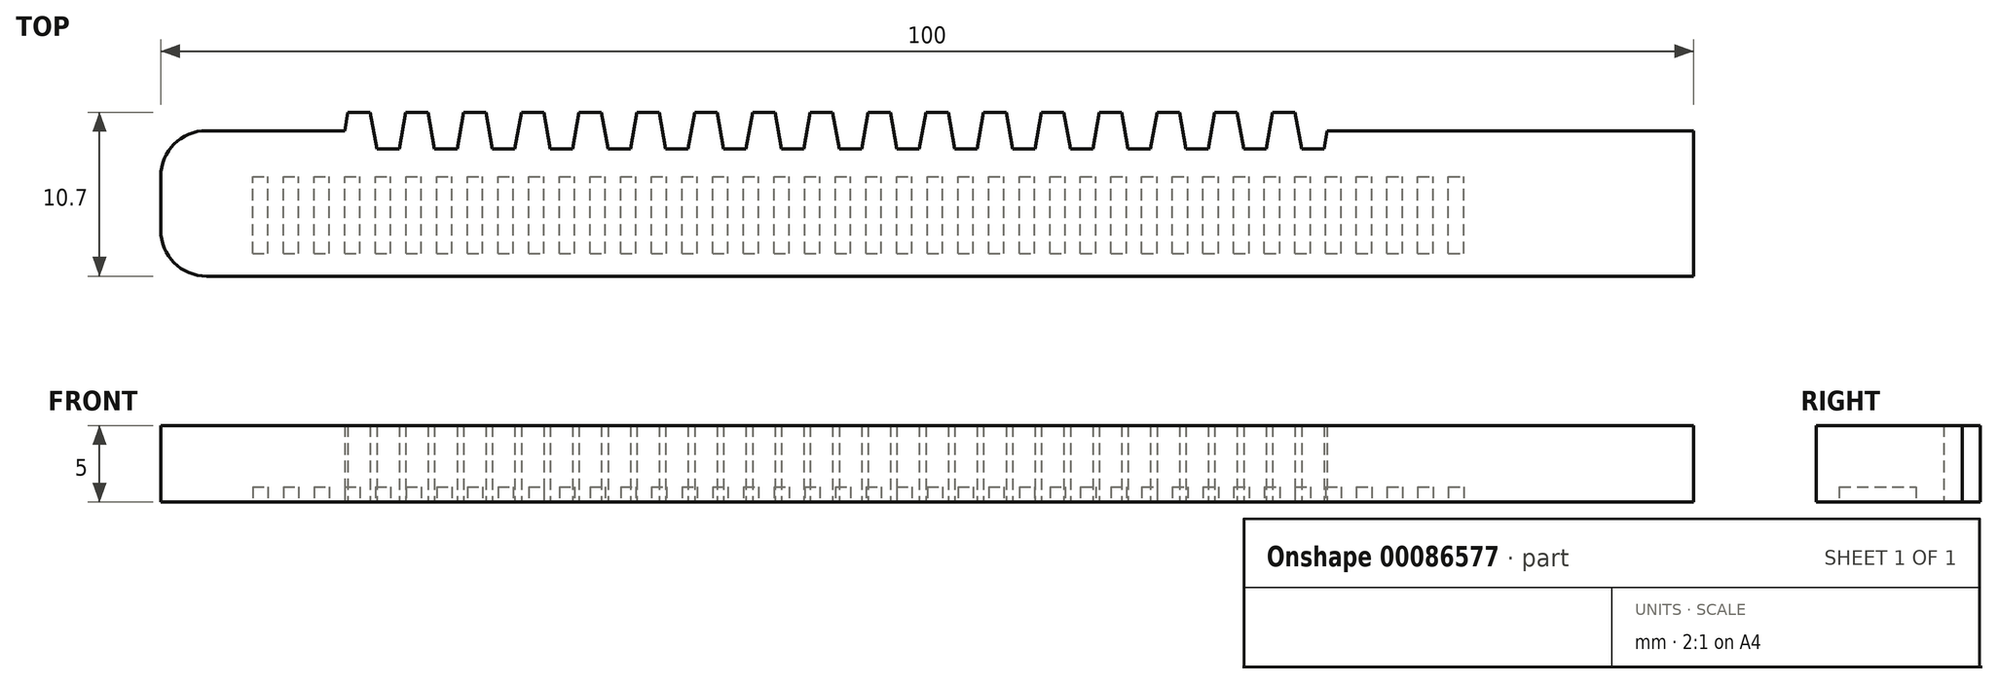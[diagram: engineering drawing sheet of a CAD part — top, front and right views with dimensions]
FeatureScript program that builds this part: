
annotation { "Feature Type Name" : "Feature", "Feature Type Description" : "" }
export const myFeature = defineFeature(function(context is Context, id is Id, definition is map)
    precondition{}
    {
        {
            var Q0;
            Q0=qCreatedBy(makeId("Top.planeOp"),FACE);
            var sketch = newSketch(context, id + "F0", { "sketchPlane" : qUnion([Q0])});
            skLineSegment(sketch, "E0", {"start": v(0, 0) * mm, "end": v(12, 0) * mm});
            skLineSegment(sketch, "E1", {"start": v(12, 0) * mm, "end": v(78, 0) * mm});
            skLineSegment(sketch, "E2", {"start": v(78, 0) * mm, "end": v(100, 0) * mm});
            skLineSegment(sketch, "E3", {"start": v(100, 0) * mm, "end": v(100, 9.5) * mm});
            skLineSegment(sketch, "E4", {"start": v(0, 0) * mm, "end": v(0, 9.5) * mm});
            skLineSegment(sketch, "E5", {"start": v(0, 9.5) * mm, "end": v(100, 9.5) * mm, "construction": true});
            skLineSegment(sketch, "E6", {"start": v(0, 9.5) * mm, "end": v(12, 9.5) * mm});
            skLineSegment(sketch, "E7", {"start": v(12, 9.5) * mm, "end": v(12.21, 10.7) * mm});
            skLineSegment(sketch, "E8", {"start": v(12.21, 10.7) * mm, "end": v(13.67, 10.7) * mm});
            skLineSegment(sketch, "E9", {"start": v(13.67, 10.7) * mm, "end": v(14.1, 8.3) * mm});
            skLineSegment(sketch, "E10", {"start": v(14.1, 8.3) * mm, "end": v(15.56, 8.3) * mm});
            skLineSegment(sketch, "E11", {"start": v(15.56, 8.3) * mm, "end": v(15.77, 9.5) * mm});
            skLineSegment(sketch, "E12.1.0.0", {"start": v(15.77, 9.5) * mm, "end": v(15.98, 10.7) * mm});
            skLineSegment(sketch, "E12.1.0.1", {"start": v(17.44, 10.7) * mm, "end": v(17.87, 8.3) * mm});
            skLineSegment(sketch, "E12.1.0.2", {"start": v(19.33, 8.3) * mm, "end": v(19.54, 9.5) * mm});
            skLineSegment(sketch, "E12.1.0.3", {"start": v(15.98, 10.7) * mm, "end": v(17.44, 10.7) * mm});
            skLineSegment(sketch, "E12.1.0.4", {"start": v(17.87, 8.3) * mm, "end": v(19.33, 8.3) * mm});
            skLineSegment(sketch, "E12.2.0.0", {"start": v(19.54, 9.5) * mm, "end": v(19.75, 10.7) * mm});
            skLineSegment(sketch, "E12.2.0.1", {"start": v(21.21, 10.7) * mm, "end": v(21.64, 8.3) * mm});
            skLineSegment(sketch, "E12.2.0.2", {"start": v(23.1, 8.3) * mm, "end": v(23.31, 9.5) * mm});
            skLineSegment(sketch, "E12.2.0.3", {"start": v(19.75, 10.7) * mm, "end": v(21.21, 10.7) * mm});
            skLineSegment(sketch, "E12.2.0.4", {"start": v(21.64, 8.3) * mm, "end": v(23.1, 8.3) * mm});
            skLineSegment(sketch, "E12.3.0.0", {"start": v(23.31, 9.5) * mm, "end": v(23.52, 10.7) * mm});
            skLineSegment(sketch, "E12.3.0.1", {"start": v(24.98, 10.7) * mm, "end": v(25.4, 8.3) * mm});
            skLineSegment(sketch, "E12.3.0.2", {"start": v(26.87, 8.3) * mm, "end": v(27.08, 9.5) * mm});
            skLineSegment(sketch, "E12.3.0.3", {"start": v(23.52, 10.7) * mm, "end": v(24.98, 10.7) * mm});
            skLineSegment(sketch, "E12.3.0.4", {"start": v(25.4, 8.3) * mm, "end": v(26.87, 8.3) * mm});
            skLineSegment(sketch, "E12.4.0.0", {"start": v(27.08, 9.5) * mm, "end": v(27.3, 10.7) * mm});
            skLineSegment(sketch, "E12.4.0.1", {"start": v(28.75, 10.7) * mm, "end": v(29.18, 8.3) * mm});
            skLineSegment(sketch, "E12.4.0.2", {"start": v(30.64, 8.3) * mm, "end": v(30.85, 9.5) * mm});
            skLineSegment(sketch, "E12.4.0.3", {"start": v(27.3, 10.7) * mm, "end": v(28.75, 10.7) * mm});
            skLineSegment(sketch, "E12.4.0.4", {"start": v(29.18, 8.3) * mm, "end": v(30.64, 8.3) * mm});
            skLineSegment(sketch, "E12.5.0.0", {"start": v(30.85, 9.5) * mm, "end": v(31.06, 10.7) * mm});
            skLineSegment(sketch, "E12.5.0.1", {"start": v(32.52, 10.7) * mm, "end": v(32.95, 8.3) * mm});
            skLineSegment(sketch, "E12.5.0.2", {"start": v(34.4, 8.3) * mm, "end": v(34.62, 9.5) * mm});
            skLineSegment(sketch, "E12.5.0.3", {"start": v(31.06, 10.7) * mm, "end": v(32.52, 10.7) * mm});
            skLineSegment(sketch, "E12.5.0.4", {"start": v(32.95, 8.3) * mm, "end": v(34.4, 8.3) * mm});
            skLineSegment(sketch, "E12.6.0.0", {"start": v(34.62, 9.5) * mm, "end": v(34.83, 10.7) * mm});
            skLineSegment(sketch, "E12.6.0.1", {"start": v(36.3, 10.7) * mm, "end": v(36.72, 8.3) * mm});
            skLineSegment(sketch, "E12.6.0.2", {"start": v(38.18, 8.3) * mm, "end": v(38.4, 9.5) * mm});
            skLineSegment(sketch, "E12.6.0.3", {"start": v(34.83, 10.7) * mm, "end": v(36.3, 10.7) * mm});
            skLineSegment(sketch, "E12.6.0.4", {"start": v(36.72, 8.3) * mm, "end": v(38.18, 8.3) * mm});
            skLineSegment(sketch, "E12.7.0.0", {"start": v(38.4, 9.5) * mm, "end": v(38.6, 10.7) * mm});
            skLineSegment(sketch, "E12.7.0.1", {"start": v(40.06, 10.7) * mm, "end": v(40.49, 8.3) * mm});
            skLineSegment(sketch, "E12.7.0.2", {"start": v(41.95, 8.3) * mm, "end": v(42.16, 9.5) * mm});
            skLineSegment(sketch, "E12.7.0.3", {"start": v(38.6, 10.7) * mm, "end": v(40.06, 10.7) * mm});
            skLineSegment(sketch, "E12.7.0.4", {"start": v(40.49, 8.3) * mm, "end": v(41.95, 8.3) * mm});
            skLineSegment(sketch, "E12.8.0.0", {"start": v(42.16, 9.5) * mm, "end": v(42.37, 10.7) * mm});
            skLineSegment(sketch, "E12.8.0.1", {"start": v(43.83, 10.7) * mm, "end": v(44.26, 8.3) * mm});
            skLineSegment(sketch, "E12.8.0.2", {"start": v(45.72, 8.3) * mm, "end": v(45.93, 9.5) * mm});
            skLineSegment(sketch, "E12.8.0.3", {"start": v(42.37, 10.7) * mm, "end": v(43.83, 10.7) * mm});
            skLineSegment(sketch, "E12.8.0.4", {"start": v(44.26, 8.3) * mm, "end": v(45.72, 8.3) * mm});
            skLineSegment(sketch, "E12.9.0.0", {"start": v(45.93, 9.5) * mm, "end": v(46.14, 10.7) * mm});
            skLineSegment(sketch, "E12.9.0.1", {"start": v(47.6, 10.7) * mm, "end": v(48.03, 8.3) * mm});
            skLineSegment(sketch, "E12.9.0.2", {"start": v(49.49, 8.3) * mm, "end": v(49.7, 9.5) * mm});
            skLineSegment(sketch, "E12.9.0.3", {"start": v(46.14, 10.7) * mm, "end": v(47.6, 10.7) * mm});
            skLineSegment(sketch, "E12.9.0.4", {"start": v(48.03, 8.3) * mm, "end": v(49.49, 8.3) * mm});
            skLineSegment(sketch, "E12.10.0.0", {"start": v(49.7, 9.5) * mm, "end": v(49.91, 10.7) * mm});
            skLineSegment(sketch, "E12.10.0.1", {"start": v(51.37, 10.7) * mm, "end": v(51.8, 8.3) * mm});
            skLineSegment(sketch, "E12.10.0.2", {"start": v(53.26, 8.3) * mm, "end": v(53.47, 9.5) * mm});
            skLineSegment(sketch, "E12.10.0.3", {"start": v(49.91, 10.7) * mm, "end": v(51.37, 10.7) * mm});
            skLineSegment(sketch, "E12.10.0.4", {"start": v(51.8, 8.3) * mm, "end": v(53.26, 8.3) * mm});
            skLineSegment(sketch, "E12.11.0.0", {"start": v(53.47, 9.5) * mm, "end": v(53.68, 10.7) * mm});
            skLineSegment(sketch, "E12.11.0.1", {"start": v(55.14, 10.7) * mm, "end": v(55.57, 8.3) * mm});
            skLineSegment(sketch, "E12.11.0.2", {"start": v(57.03, 8.3) * mm, "end": v(57.24, 9.5) * mm});
            skLineSegment(sketch, "E12.11.0.3", {"start": v(53.68, 10.7) * mm, "end": v(55.14, 10.7) * mm});
            skLineSegment(sketch, "E12.11.0.4", {"start": v(55.57, 8.3) * mm, "end": v(57.03, 8.3) * mm});
            skLineSegment(sketch, "E12.12.0.0", {"start": v(57.24, 9.5) * mm, "end": v(57.45, 10.7) * mm});
            skLineSegment(sketch, "E12.12.0.1", {"start": v(58.91, 10.7) * mm, "end": v(59.34, 8.3) * mm});
            skLineSegment(sketch, "E12.12.0.2", {"start": v(60.8, 8.3) * mm, "end": v(61.01, 9.5) * mm});
            skLineSegment(sketch, "E12.12.0.3", {"start": v(57.45, 10.7) * mm, "end": v(58.91, 10.7) * mm});
            skLineSegment(sketch, "E12.12.0.4", {"start": v(59.34, 8.3) * mm, "end": v(60.8, 8.3) * mm});
            skLineSegment(sketch, "E12.13.0.0", {"start": v(61.01, 9.5) * mm, "end": v(61.22, 10.7) * mm});
            skLineSegment(sketch, "E12.13.0.1", {"start": v(62.68, 10.7) * mm, "end": v(63.1, 8.3) * mm});
            skLineSegment(sketch, "E12.13.0.2", {"start": v(64.57, 8.3) * mm, "end": v(64.78, 9.5) * mm});
            skLineSegment(sketch, "E12.13.0.3", {"start": v(61.22, 10.7) * mm, "end": v(62.68, 10.7) * mm});
            skLineSegment(sketch, "E12.13.0.4", {"start": v(63.1, 8.3) * mm, "end": v(64.57, 8.3) * mm});
            skLineSegment(sketch, "E12.14.0.0", {"start": v(64.78, 9.5) * mm, "end": v(65, 10.7) * mm});
            skLineSegment(sketch, "E12.14.0.1", {"start": v(66.45, 10.7) * mm, "end": v(66.88, 8.3) * mm});
            skLineSegment(sketch, "E12.14.0.2", {"start": v(68.34, 8.3) * mm, "end": v(68.55, 9.5) * mm});
            skLineSegment(sketch, "E12.14.0.3", {"start": v(65, 10.7) * mm, "end": v(66.45, 10.7) * mm});
            skLineSegment(sketch, "E12.14.0.4", {"start": v(66.88, 8.3) * mm, "end": v(68.34, 8.3) * mm});
            skLineSegment(sketch, "E12.15.0.0", {"start": v(68.55, 9.5) * mm, "end": v(68.76, 10.7) * mm});
            skLineSegment(sketch, "E12.15.0.1", {"start": v(70.22, 10.7) * mm, "end": v(70.65, 8.3) * mm});
            skLineSegment(sketch, "E12.15.0.2", {"start": v(72.1, 8.3) * mm, "end": v(72.32, 9.5) * mm});
            skLineSegment(sketch, "E12.15.0.3", {"start": v(68.76, 10.7) * mm, "end": v(70.22, 10.7) * mm});
            skLineSegment(sketch, "E12.15.0.4", {"start": v(70.65, 8.3) * mm, "end": v(72.1, 8.3) * mm});
            skLineSegment(sketch, "E12.16.0.0", {"start": v(72.32, 9.5) * mm, "end": v(72.53, 10.7) * mm});
            skLineSegment(sketch, "E12.16.0.1", {"start": v(74, 10.7) * mm, "end": v(74.42, 8.3) * mm});
            skLineSegment(sketch, "E12.16.0.2", {"start": v(75.88, 8.3) * mm, "end": v(76.1, 9.5) * mm});
            skLineSegment(sketch, "E12.16.0.3", {"start": v(72.53, 10.7) * mm, "end": v(74, 10.7) * mm});
            skLineSegment(sketch, "E12.16.0.4", {"start": v(74.42, 8.3) * mm, "end": v(75.88, 8.3) * mm});
            skLineSegment(sketch, "E12.direction1", {"start": v(12, 9.5) * mm, "end": v(15.77, 9.5) * mm, "construction": true});
            skLineSegment(sketch, "E13", {"start": v(76.1, 9.5) * mm, "end": v(100, 9.5) * mm});
            skSolve(sketch);
        }
        {
            var Q0;
            Q0 = qSketchRegion(id + "F0", true);
            extrude(context, id + "F1", {"entities" : qUnion([Q0]), "depth" : 5 * mm});
        }
        {
            var Q0;
            Q0=makeQuery(id+"F1.opExtrude","SWEPT_EDGE",EDGE,{"disambiguationData":[OSD([sQuery(id+"F0.wireOp",EDGE,"E0"),sQuery(id+"F0.wireOp",EDGE,"E4")])]});
            var Q1;
            Q1=makeQuery(id+"F1.opExtrude","SWEPT_EDGE",EDGE,{"disambiguationData":[OSD([sQuery(id+"F0.wireOp",EDGE,"E4"),sQuery(id+"F0.wireOp",EDGE,"E6")])]});
            fillet(context, id + "F2", {"entities" : qUnion([Q0, Q1]), "radius" : 3 * mm, "tangentPropagation" : true, "allowEdgeOverflow" : false});
        }
        {
            var Q0;
            Q0=makeQuery(id+"F1.opExtrude","CAP_FACE",FACE,{"disambiguationData":[OSD([sQuery(id+"F0.wireOp",EDGE,"E0"),sQuery(id+"F0.wireOp",EDGE,"E1"),sQuery(id+"F0.wireOp",EDGE,"E2"),sQuery(id+"F0.wireOp",EDGE,"E3"),sQuery(id+"F0.wireOp",EDGE,"E4"),sQuery(id+"F0.wireOp",EDGE,"E6"),sQuery(id+"F0.wireOp",EDGE,"E7"),sQuery(id+"F0.wireOp",EDGE,"E8"),sQuery(id+"F0.wireOp",EDGE,"E9"),sQuery(id+"F0.wireOp",EDGE,"E10"),sQuery(id+"F0.wireOp",EDGE,"E11"),sQuery(id+"F0.wireOp",EDGE,"E12.1.0.0"),sQuery(id+"F0.wireOp",EDGE,"E12.1.0.1"),sQuery(id+"F0.wireOp",EDGE,"E12.1.0.2"),sQuery(id+"F0.wireOp",EDGE,"E12.1.0.3"),sQuery(id+"F0.wireOp",EDGE,"E12.1.0.4"),sQuery(id+"F0.wireOp",EDGE,"E12.2.0.0"),sQuery(id+"F0.wireOp",EDGE,"E12.2.0.1"),sQuery(id+"F0.wireOp",EDGE,"E12.2.0.2"),sQuery(id+"F0.wireOp",EDGE,"E12.2.0.3"),sQuery(id+"F0.wireOp",EDGE,"E12.2.0.4"),sQuery(id+"F0.wireOp",EDGE,"E12.3.0.0"),sQuery(id+"F0.wireOp",EDGE,"E12.3.0.1"),sQuery(id+"F0.wireOp",EDGE,"E12.3.0.2"),sQuery(id+"F0.wireOp",EDGE,"E12.3.0.3"),sQuery(id+"F0.wireOp",EDGE,"E12.3.0.4"),sQuery(id+"F0.wireOp",EDGE,"E12.4.0.0"),sQuery(id+"F0.wireOp",EDGE,"E12.4.0.1"),sQuery(id+"F0.wireOp",EDGE,"E12.4.0.2"),sQuery(id+"F0.wireOp",EDGE,"E12.4.0.3"),sQuery(id+"F0.wireOp",EDGE,"E12.4.0.4"),sQuery(id+"F0.wireOp",EDGE,"E12.5.0.0"),sQuery(id+"F0.wireOp",EDGE,"E12.5.0.1"),sQuery(id+"F0.wireOp",EDGE,"E12.5.0.2"),sQuery(id+"F0.wireOp",EDGE,"E12.5.0.3"),sQuery(id+"F0.wireOp",EDGE,"E12.5.0.4"),sQuery(id+"F0.wireOp",EDGE,"E12.6.0.0"),sQuery(id+"F0.wireOp",EDGE,"E12.6.0.1"),sQuery(id+"F0.wireOp",EDGE,"E12.6.0.2"),sQuery(id+"F0.wireOp",EDGE,"E12.6.0.3"),sQuery(id+"F0.wireOp",EDGE,"E12.6.0.4"),sQuery(id+"F0.wireOp",EDGE,"E12.7.0.0"),sQuery(id+"F0.wireOp",EDGE,"E12.7.0.1"),sQuery(id+"F0.wireOp",EDGE,"E12.7.0.2"),sQuery(id+"F0.wireOp",EDGE,"E12.7.0.3"),sQuery(id+"F0.wireOp",EDGE,"E12.7.0.4"),sQuery(id+"F0.wireOp",EDGE,"E12.8.0.0"),sQuery(id+"F0.wireOp",EDGE,"E12.8.0.1"),sQuery(id+"F0.wireOp",EDGE,"E12.8.0.2"),sQuery(id+"F0.wireOp",EDGE,"E12.8.0.3"),sQuery(id+"F0.wireOp",EDGE,"E12.8.0.4"),sQuery(id+"F0.wireOp",EDGE,"E12.9.0.0"),sQuery(id+"F0.wireOp",EDGE,"E12.9.0.1"),sQuery(id+"F0.wireOp",EDGE,"E12.9.0.2"),sQuery(id+"F0.wireOp",EDGE,"E12.9.0.3"),sQuery(id+"F0.wireOp",EDGE,"E12.9.0.4"),sQuery(id+"F0.wireOp",EDGE,"E12.10.0.0"),sQuery(id+"F0.wireOp",EDGE,"E12.10.0.1"),sQuery(id+"F0.wireOp",EDGE,"E12.10.0.2"),sQuery(id+"F0.wireOp",EDGE,"E12.10.0.3"),sQuery(id+"F0.wireOp",EDGE,"E12.10.0.4"),sQuery(id+"F0.wireOp",EDGE,"E12.11.0.0"),sQuery(id+"F0.wireOp",EDGE,"E12.11.0.1"),sQuery(id+"F0.wireOp",EDGE,"E12.11.0.2"),sQuery(id+"F0.wireOp",EDGE,"E12.11.0.3"),sQuery(id+"F0.wireOp",EDGE,"E12.11.0.4"),sQuery(id+"F0.wireOp",EDGE,"E12.12.0.0"),sQuery(id+"F0.wireOp",EDGE,"E12.12.0.1"),sQuery(id+"F0.wireOp",EDGE,"E12.12.0.2"),sQuery(id+"F0.wireOp",EDGE,"E12.12.0.3"),sQuery(id+"F0.wireOp",EDGE,"E12.12.0.4"),sQuery(id+"F0.wireOp",EDGE,"E12.13.0.0"),sQuery(id+"F0.wireOp",EDGE,"E12.13.0.1"),sQuery(id+"F0.wireOp",EDGE,"E12.13.0.2"),sQuery(id+"F0.wireOp",EDGE,"E12.13.0.3"),sQuery(id+"F0.wireOp",EDGE,"E12.13.0.4"),sQuery(id+"F0.wireOp",EDGE,"E12.14.0.0"),sQuery(id+"F0.wireOp",EDGE,"E12.14.0.1"),sQuery(id+"F0.wireOp",EDGE,"E12.14.0.2"),sQuery(id+"F0.wireOp",EDGE,"E12.14.0.3"),sQuery(id+"F0.wireOp",EDGE,"E12.14.0.4"),sQuery(id+"F0.wireOp",EDGE,"E12.15.0.0"),sQuery(id+"F0.wireOp",EDGE,"E12.15.0.1"),sQuery(id+"F0.wireOp",EDGE,"E12.15.0.2"),sQuery(id+"F0.wireOp",EDGE,"E12.15.0.3"),sQuery(id+"F0.wireOp",EDGE,"E12.15.0.4"),sQuery(id+"F0.wireOp",EDGE,"E12.16.0.0"),sQuery(id+"F0.wireOp",EDGE,"E12.16.0.1"),sQuery(id+"F0.wireOp",EDGE,"E12.16.0.2"),sQuery(id+"F0.wireOp",EDGE,"E12.16.0.3"),sQuery(id+"F0.wireOp",EDGE,"E12.16.0.4"),sQuery(id+"F0.wireOp",EDGE,"E13")])],"isStart":true});
            var sketch = newSketch(context, id + "F3", { "sketchPlane" : qUnion([Q0])});
            skLineSegment(sketch, "E14", {"start": v(100, -4) * mm, "end": v(0, -4) * mm, "construction": true});
            skLineSegment(sketch, "E15.bottom", {"start": v(84, -1.5) * mm, "end": v(85, -1.5) * mm});
            skLineSegment(sketch, "E15.top", {"start": v(84, -6.5) * mm, "end": v(85, -6.5) * mm});
            skLineSegment(sketch, "E15.left", {"start": v(84, -1.5) * mm, "end": v(84, -6.5) * mm});
            skLineSegment(sketch, "E15.right", {"start": v(85, -1.5) * mm, "end": v(85, -6.5) * mm});
            skPoint(sketch, "E15.middle", {"position": v(84.5, -4) * mm});
            skPoint(sketch, "E16.1.0.0", {"position": v(82.5, -4) * mm});
            skLineSegment(sketch, "E16.1.0.1", {"start": v(83, -1.5) * mm, "end": v(83, -6.5) * mm});
            skLineSegment(sketch, "E16.1.0.2", {"start": v(82, -1.5) * mm, "end": v(82, -6.5) * mm});
            skLineSegment(sketch, "E16.1.0.3", {"start": v(82, -6.5) * mm, "end": v(83, -6.5) * mm});
            skLineSegment(sketch, "E16.1.0.4", {"start": v(82, -1.5) * mm, "end": v(83, -1.5) * mm});
            skPoint(sketch, "E16.2.0.0", {"position": v(80.5, -4) * mm});
            skLineSegment(sketch, "E16.2.0.1", {"start": v(81, -1.5) * mm, "end": v(81, -6.5) * mm});
            skLineSegment(sketch, "E16.2.0.2", {"start": v(80, -1.5) * mm, "end": v(80, -6.5) * mm});
            skLineSegment(sketch, "E16.2.0.3", {"start": v(80, -6.5) * mm, "end": v(81, -6.5) * mm});
            skLineSegment(sketch, "E16.2.0.4", {"start": v(80, -1.5) * mm, "end": v(81, -1.5) * mm});
            skPoint(sketch, "E16.3.0.0", {"position": v(78.5, -4) * mm});
            skLineSegment(sketch, "E16.3.0.1", {"start": v(79, -1.5) * mm, "end": v(79, -6.5) * mm});
            skLineSegment(sketch, "E16.3.0.2", {"start": v(78, -1.5) * mm, "end": v(78, -6.5) * mm});
            skLineSegment(sketch, "E16.3.0.3", {"start": v(78, -6.5) * mm, "end": v(79, -6.5) * mm});
            skLineSegment(sketch, "E16.3.0.4", {"start": v(78, -1.5) * mm, "end": v(79, -1.5) * mm});
            skPoint(sketch, "E16.4.0.0", {"position": v(76.5, -4) * mm});
            skLineSegment(sketch, "E16.4.0.1", {"start": v(77, -1.5) * mm, "end": v(77, -6.5) * mm});
            skLineSegment(sketch, "E16.4.0.2", {"start": v(76, -1.5) * mm, "end": v(76, -6.5) * mm});
            skLineSegment(sketch, "E16.4.0.3", {"start": v(76, -6.5) * mm, "end": v(77, -6.5) * mm});
            skLineSegment(sketch, "E16.4.0.4", {"start": v(76, -1.5) * mm, "end": v(77, -1.5) * mm});
            skPoint(sketch, "E16.5.0.0", {"position": v(74.5, -4) * mm});
            skLineSegment(sketch, "E16.5.0.1", {"start": v(75, -1.5) * mm, "end": v(75, -6.5) * mm});
            skLineSegment(sketch, "E16.5.0.2", {"start": v(74, -1.5) * mm, "end": v(74, -6.5) * mm});
            skLineSegment(sketch, "E16.5.0.3", {"start": v(74, -6.5) * mm, "end": v(75, -6.5) * mm});
            skLineSegment(sketch, "E16.5.0.4", {"start": v(74, -1.5) * mm, "end": v(75, -1.5) * mm});
            skPoint(sketch, "E16.6.0.0", {"position": v(72.5, -4) * mm});
            skLineSegment(sketch, "E16.6.0.1", {"start": v(73, -1.5) * mm, "end": v(73, -6.5) * mm});
            skLineSegment(sketch, "E16.6.0.2", {"start": v(72, -1.5) * mm, "end": v(72, -6.5) * mm});
            skLineSegment(sketch, "E16.6.0.3", {"start": v(72, -6.5) * mm, "end": v(73, -6.5) * mm});
            skLineSegment(sketch, "E16.6.0.4", {"start": v(72, -1.5) * mm, "end": v(73, -1.5) * mm});
            skPoint(sketch, "E16.7.0.0", {"position": v(70.5, -4) * mm});
            skLineSegment(sketch, "E16.7.0.1", {"start": v(71, -1.5) * mm, "end": v(71, -6.5) * mm});
            skLineSegment(sketch, "E16.7.0.2", {"start": v(70, -1.5) * mm, "end": v(70, -6.5) * mm});
            skLineSegment(sketch, "E16.7.0.3", {"start": v(70, -6.5) * mm, "end": v(71, -6.5) * mm});
            skLineSegment(sketch, "E16.7.0.4", {"start": v(70, -1.5) * mm, "end": v(71, -1.5) * mm});
            skPoint(sketch, "E16.8.0.0", {"position": v(68.5, -4) * mm});
            skLineSegment(sketch, "E16.8.0.1", {"start": v(69, -1.5) * mm, "end": v(69, -6.5) * mm});
            skLineSegment(sketch, "E16.8.0.2", {"start": v(68, -1.5) * mm, "end": v(68, -6.5) * mm});
            skLineSegment(sketch, "E16.8.0.3", {"start": v(68, -6.5) * mm, "end": v(69, -6.5) * mm});
            skLineSegment(sketch, "E16.8.0.4", {"start": v(68, -1.5) * mm, "end": v(69, -1.5) * mm});
            skPoint(sketch, "E16.9.0.0", {"position": v(66.5, -4) * mm});
            skLineSegment(sketch, "E16.9.0.1", {"start": v(67, -1.5) * mm, "end": v(67, -6.5) * mm});
            skLineSegment(sketch, "E16.9.0.2", {"start": v(66, -1.5) * mm, "end": v(66, -6.5) * mm});
            skLineSegment(sketch, "E16.9.0.3", {"start": v(66, -6.5) * mm, "end": v(67, -6.5) * mm});
            skLineSegment(sketch, "E16.9.0.4", {"start": v(66, -1.5) * mm, "end": v(67, -1.5) * mm});
            skPoint(sketch, "E16.10.0.0", {"position": v(64.5, -4) * mm});
            skLineSegment(sketch, "E16.10.0.1", {"start": v(65, -1.5) * mm, "end": v(65, -6.5) * mm});
            skLineSegment(sketch, "E16.10.0.2", {"start": v(64, -1.5) * mm, "end": v(64, -6.5) * mm});
            skLineSegment(sketch, "E16.10.0.3", {"start": v(64, -6.5) * mm, "end": v(65, -6.5) * mm});
            skLineSegment(sketch, "E16.10.0.4", {"start": v(64, -1.5) * mm, "end": v(65, -1.5) * mm});
            skPoint(sketch, "E16.11.0.0", {"position": v(62.5, -4) * mm});
            skLineSegment(sketch, "E16.11.0.1", {"start": v(63, -1.5) * mm, "end": v(63, -6.5) * mm});
            skLineSegment(sketch, "E16.11.0.2", {"start": v(62, -1.5) * mm, "end": v(62, -6.5) * mm});
            skLineSegment(sketch, "E16.11.0.3", {"start": v(62, -6.5) * mm, "end": v(63, -6.5) * mm});
            skLineSegment(sketch, "E16.11.0.4", {"start": v(62, -1.5) * mm, "end": v(63, -1.5) * mm});
            skPoint(sketch, "E16.12.0.0", {"position": v(60.5, -4) * mm});
            skLineSegment(sketch, "E16.12.0.1", {"start": v(61, -1.5) * mm, "end": v(61, -6.5) * mm});
            skLineSegment(sketch, "E16.12.0.2", {"start": v(60, -1.5) * mm, "end": v(60, -6.5) * mm});
            skLineSegment(sketch, "E16.12.0.3", {"start": v(60, -6.5) * mm, "end": v(61, -6.5) * mm});
            skLineSegment(sketch, "E16.12.0.4", {"start": v(60, -1.5) * mm, "end": v(61, -1.5) * mm});
            skPoint(sketch, "E16.13.0.0", {"position": v(58.5, -4) * mm});
            skLineSegment(sketch, "E16.13.0.1", {"start": v(59, -1.5) * mm, "end": v(59, -6.5) * mm});
            skLineSegment(sketch, "E16.13.0.2", {"start": v(58, -1.5) * mm, "end": v(58, -6.5) * mm});
            skLineSegment(sketch, "E16.13.0.3", {"start": v(58, -6.5) * mm, "end": v(59, -6.5) * mm});
            skLineSegment(sketch, "E16.13.0.4", {"start": v(58, -1.5) * mm, "end": v(59, -1.5) * mm});
            skPoint(sketch, "E16.14.0.0", {"position": v(56.5, -4) * mm});
            skLineSegment(sketch, "E16.14.0.1", {"start": v(57, -1.5) * mm, "end": v(57, -6.5) * mm});
            skLineSegment(sketch, "E16.14.0.2", {"start": v(56, -1.5) * mm, "end": v(56, -6.5) * mm});
            skLineSegment(sketch, "E16.14.0.3", {"start": v(56, -6.5) * mm, "end": v(57, -6.5) * mm});
            skLineSegment(sketch, "E16.14.0.4", {"start": v(56, -1.5) * mm, "end": v(57, -1.5) * mm});
            skPoint(sketch, "E16.15.0.0", {"position": v(54.5, -4) * mm});
            skLineSegment(sketch, "E16.15.0.1", {"start": v(55, -1.5) * mm, "end": v(55, -6.5) * mm});
            skLineSegment(sketch, "E16.15.0.2", {"start": v(54, -1.5) * mm, "end": v(54, -6.5) * mm});
            skLineSegment(sketch, "E16.15.0.3", {"start": v(54, -6.5) * mm, "end": v(55, -6.5) * mm});
            skLineSegment(sketch, "E16.15.0.4", {"start": v(54, -1.5) * mm, "end": v(55, -1.5) * mm});
            skPoint(sketch, "E16.16.0.0", {"position": v(52.5, -4) * mm});
            skLineSegment(sketch, "E16.16.0.1", {"start": v(53, -1.5) * mm, "end": v(53, -6.5) * mm});
            skLineSegment(sketch, "E16.16.0.2", {"start": v(52, -1.5) * mm, "end": v(52, -6.5) * mm});
            skLineSegment(sketch, "E16.16.0.3", {"start": v(52, -6.5) * mm, "end": v(53, -6.5) * mm});
            skLineSegment(sketch, "E16.16.0.4", {"start": v(52, -1.5) * mm, "end": v(53, -1.5) * mm});
            skPoint(sketch, "E16.17.0.0", {"position": v(50.5, -4) * mm});
            skLineSegment(sketch, "E16.17.0.1", {"start": v(51, -1.5) * mm, "end": v(51, -6.5) * mm});
            skLineSegment(sketch, "E16.17.0.2", {"start": v(50, -1.5) * mm, "end": v(50, -6.5) * mm});
            skLineSegment(sketch, "E16.17.0.3", {"start": v(50, -6.5) * mm, "end": v(51, -6.5) * mm});
            skLineSegment(sketch, "E16.17.0.4", {"start": v(50, -1.5) * mm, "end": v(51, -1.5) * mm});
            skPoint(sketch, "E16.18.0.0", {"position": v(48.5, -4) * mm});
            skLineSegment(sketch, "E16.18.0.1", {"start": v(49, -1.5) * mm, "end": v(49, -6.5) * mm});
            skLineSegment(sketch, "E16.18.0.2", {"start": v(48, -1.5) * mm, "end": v(48, -6.5) * mm});
            skLineSegment(sketch, "E16.18.0.3", {"start": v(48, -6.5) * mm, "end": v(49, -6.5) * mm});
            skLineSegment(sketch, "E16.18.0.4", {"start": v(48, -1.5) * mm, "end": v(49, -1.5) * mm});
            skPoint(sketch, "E16.19.0.0", {"position": v(46.5, -4) * mm});
            skLineSegment(sketch, "E16.19.0.1", {"start": v(47, -1.5) * mm, "end": v(47, -6.5) * mm});
            skLineSegment(sketch, "E16.19.0.2", {"start": v(46, -1.5) * mm, "end": v(46, -6.5) * mm});
            skLineSegment(sketch, "E16.19.0.3", {"start": v(46, -6.5) * mm, "end": v(47, -6.5) * mm});
            skLineSegment(sketch, "E16.19.0.4", {"start": v(46, -1.5) * mm, "end": v(47, -1.5) * mm});
            skPoint(sketch, "E16.20.0.0", {"position": v(44.5, -4) * mm});
            skLineSegment(sketch, "E16.20.0.1", {"start": v(45, -1.5) * mm, "end": v(45, -6.5) * mm});
            skLineSegment(sketch, "E16.20.0.2", {"start": v(44, -1.5) * mm, "end": v(44, -6.5) * mm});
            skLineSegment(sketch, "E16.20.0.3", {"start": v(44, -6.5) * mm, "end": v(45, -6.5) * mm});
            skLineSegment(sketch, "E16.20.0.4", {"start": v(44, -1.5) * mm, "end": v(45, -1.5) * mm});
            skPoint(sketch, "E16.21.0.0", {"position": v(42.5, -4) * mm});
            skLineSegment(sketch, "E16.21.0.1", {"start": v(43, -1.5) * mm, "end": v(43, -6.5) * mm});
            skLineSegment(sketch, "E16.21.0.2", {"start": v(42, -1.5) * mm, "end": v(42, -6.5) * mm});
            skLineSegment(sketch, "E16.21.0.3", {"start": v(42, -6.5) * mm, "end": v(43, -6.5) * mm});
            skLineSegment(sketch, "E16.21.0.4", {"start": v(42, -1.5) * mm, "end": v(43, -1.5) * mm});
            skPoint(sketch, "E16.22.0.0", {"position": v(40.5, -4) * mm});
            skLineSegment(sketch, "E16.22.0.1", {"start": v(41, -1.5) * mm, "end": v(41, -6.5) * mm});
            skLineSegment(sketch, "E16.22.0.2", {"start": v(40, -1.5) * mm, "end": v(40, -6.5) * mm});
            skLineSegment(sketch, "E16.22.0.3", {"start": v(40, -6.5) * mm, "end": v(41, -6.5) * mm});
            skLineSegment(sketch, "E16.22.0.4", {"start": v(40, -1.5) * mm, "end": v(41, -1.5) * mm});
            skPoint(sketch, "E16.23.0.0", {"position": v(38.5, -4) * mm});
            skLineSegment(sketch, "E16.23.0.1", {"start": v(39, -1.5) * mm, "end": v(39, -6.5) * mm});
            skLineSegment(sketch, "E16.23.0.2", {"start": v(38, -1.5) * mm, "end": v(38, -6.5) * mm});
            skLineSegment(sketch, "E16.23.0.3", {"start": v(38, -6.5) * mm, "end": v(39, -6.5) * mm});
            skLineSegment(sketch, "E16.23.0.4", {"start": v(38, -1.5) * mm, "end": v(39, -1.5) * mm});
            skPoint(sketch, "E16.24.0.0", {"position": v(36.5, -4) * mm});
            skLineSegment(sketch, "E16.24.0.1", {"start": v(37, -1.5) * mm, "end": v(37, -6.5) * mm});
            skLineSegment(sketch, "E16.24.0.2", {"start": v(36, -1.5) * mm, "end": v(36, -6.5) * mm});
            skLineSegment(sketch, "E16.24.0.3", {"start": v(36, -6.5) * mm, "end": v(37, -6.5) * mm});
            skLineSegment(sketch, "E16.24.0.4", {"start": v(36, -1.5) * mm, "end": v(37, -1.5) * mm});
            skPoint(sketch, "E16.25.0.0", {"position": v(34.5, -4) * mm});
            skLineSegment(sketch, "E16.25.0.1", {"start": v(35, -1.5) * mm, "end": v(35, -6.5) * mm});
            skLineSegment(sketch, "E16.25.0.2", {"start": v(34, -1.5) * mm, "end": v(34, -6.5) * mm});
            skLineSegment(sketch, "E16.25.0.3", {"start": v(34, -6.5) * mm, "end": v(35, -6.5) * mm});
            skLineSegment(sketch, "E16.25.0.4", {"start": v(34, -1.5) * mm, "end": v(35, -1.5) * mm});
            skPoint(sketch, "E16.26.0.0", {"position": v(32.5, -4) * mm});
            skLineSegment(sketch, "E16.26.0.1", {"start": v(33, -1.5) * mm, "end": v(33, -6.5) * mm});
            skLineSegment(sketch, "E16.26.0.2", {"start": v(32, -1.5) * mm, "end": v(32, -6.5) * mm});
            skLineSegment(sketch, "E16.26.0.3", {"start": v(32, -6.5) * mm, "end": v(33, -6.5) * mm});
            skLineSegment(sketch, "E16.26.0.4", {"start": v(32, -1.5) * mm, "end": v(33, -1.5) * mm});
            skPoint(sketch, "E16.27.0.0", {"position": v(30.5, -4) * mm});
            skLineSegment(sketch, "E16.27.0.1", {"start": v(31, -1.5) * mm, "end": v(31, -6.5) * mm});
            skLineSegment(sketch, "E16.27.0.2", {"start": v(30, -1.5) * mm, "end": v(30, -6.5) * mm});
            skLineSegment(sketch, "E16.27.0.3", {"start": v(30, -6.5) * mm, "end": v(31, -6.5) * mm});
            skLineSegment(sketch, "E16.27.0.4", {"start": v(30, -1.5) * mm, "end": v(31, -1.5) * mm});
            skPoint(sketch, "E16.28.0.0", {"position": v(28.5, -4) * mm});
            skLineSegment(sketch, "E16.28.0.1", {"start": v(29, -1.5) * mm, "end": v(29, -6.5) * mm});
            skLineSegment(sketch, "E16.28.0.2", {"start": v(28, -1.5) * mm, "end": v(28, -6.5) * mm});
            skLineSegment(sketch, "E16.28.0.3", {"start": v(28, -6.5) * mm, "end": v(29, -6.5) * mm});
            skLineSegment(sketch, "E16.28.0.4", {"start": v(28, -1.5) * mm, "end": v(29, -1.5) * mm});
            skPoint(sketch, "E16.29.0.0", {"position": v(26.5, -4) * mm});
            skLineSegment(sketch, "E16.29.0.1", {"start": v(27, -1.5) * mm, "end": v(27, -6.5) * mm});
            skLineSegment(sketch, "E16.29.0.2", {"start": v(26, -1.5) * mm, "end": v(26, -6.5) * mm});
            skLineSegment(sketch, "E16.29.0.3", {"start": v(26, -6.5) * mm, "end": v(27, -6.5) * mm});
            skLineSegment(sketch, "E16.29.0.4", {"start": v(26, -1.5) * mm, "end": v(27, -1.5) * mm});
            skPoint(sketch, "E16.30.0.0", {"position": v(24.5, -4) * mm});
            skLineSegment(sketch, "E16.30.0.1", {"start": v(25, -1.5) * mm, "end": v(25, -6.5) * mm});
            skLineSegment(sketch, "E16.30.0.2", {"start": v(24, -1.5) * mm, "end": v(24, -6.5) * mm});
            skLineSegment(sketch, "E16.30.0.3", {"start": v(24, -6.5) * mm, "end": v(25, -6.5) * mm});
            skLineSegment(sketch, "E16.30.0.4", {"start": v(24, -1.5) * mm, "end": v(25, -1.5) * mm});
            skPoint(sketch, "E16.31.0.0", {"position": v(22.5, -4) * mm});
            skLineSegment(sketch, "E16.31.0.1", {"start": v(23, -1.5) * mm, "end": v(23, -6.5) * mm});
            skLineSegment(sketch, "E16.31.0.2", {"start": v(22, -1.5) * mm, "end": v(22, -6.5) * mm});
            skLineSegment(sketch, "E16.31.0.3", {"start": v(22, -6.5) * mm, "end": v(23, -6.5) * mm});
            skLineSegment(sketch, "E16.31.0.4", {"start": v(22, -1.5) * mm, "end": v(23, -1.5) * mm});
            skPoint(sketch, "E16.32.0.0", {"position": v(20.5, -4) * mm});
            skLineSegment(sketch, "E16.32.0.1", {"start": v(21, -1.5) * mm, "end": v(21, -6.5) * mm});
            skLineSegment(sketch, "E16.32.0.2", {"start": v(20, -1.5) * mm, "end": v(20, -6.5) * mm});
            skLineSegment(sketch, "E16.32.0.3", {"start": v(20, -6.5) * mm, "end": v(21, -6.5) * mm});
            skLineSegment(sketch, "E16.32.0.4", {"start": v(20, -1.5) * mm, "end": v(21, -1.5) * mm});
            skPoint(sketch, "E16.33.0.0", {"position": v(18.5, -4) * mm});
            skLineSegment(sketch, "E16.33.0.1", {"start": v(19, -1.5) * mm, "end": v(19, -6.5) * mm});
            skLineSegment(sketch, "E16.33.0.2", {"start": v(18, -1.5) * mm, "end": v(18, -6.5) * mm});
            skLineSegment(sketch, "E16.33.0.3", {"start": v(18, -6.5) * mm, "end": v(19, -6.5) * mm});
            skLineSegment(sketch, "E16.33.0.4", {"start": v(18, -1.5) * mm, "end": v(19, -1.5) * mm});
            skPoint(sketch, "E16.34.0.0", {"position": v(16.5, -4) * mm});
            skLineSegment(sketch, "E16.34.0.1", {"start": v(17, -1.5) * mm, "end": v(17, -6.5) * mm});
            skLineSegment(sketch, "E16.34.0.2", {"start": v(16, -1.5) * mm, "end": v(16, -6.5) * mm});
            skLineSegment(sketch, "E16.34.0.3", {"start": v(16, -6.5) * mm, "end": v(17, -6.5) * mm});
            skLineSegment(sketch, "E16.34.0.4", {"start": v(16, -1.5) * mm, "end": v(17, -1.5) * mm});
            skPoint(sketch, "E16.35.0.0", {"position": v(14.5, -4) * mm});
            skLineSegment(sketch, "E16.35.0.1", {"start": v(15, -1.5) * mm, "end": v(15, -6.5) * mm});
            skLineSegment(sketch, "E16.35.0.2", {"start": v(14, -1.5) * mm, "end": v(14, -6.5) * mm});
            skLineSegment(sketch, "E16.35.0.3", {"start": v(14, -6.5) * mm, "end": v(15, -6.5) * mm});
            skLineSegment(sketch, "E16.35.0.4", {"start": v(14, -1.5) * mm, "end": v(15, -1.5) * mm});
            skPoint(sketch, "E16.36.0.0", {"position": v(12.5, -4) * mm});
            skLineSegment(sketch, "E16.36.0.1", {"start": v(13, -1.5) * mm, "end": v(13, -6.5) * mm});
            skLineSegment(sketch, "E16.36.0.2", {"start": v(12, -1.5) * mm, "end": v(12, -6.5) * mm});
            skLineSegment(sketch, "E16.36.0.3", {"start": v(12, -6.5) * mm, "end": v(13, -6.5) * mm});
            skLineSegment(sketch, "E16.36.0.4", {"start": v(12, -1.5) * mm, "end": v(13, -1.5) * mm});
            skPoint(sketch, "E16.37.0.0", {"position": v(10.5, -4) * mm});
            skLineSegment(sketch, "E16.37.0.1", {"start": v(11, -1.5) * mm, "end": v(11, -6.5) * mm});
            skLineSegment(sketch, "E16.37.0.2", {"start": v(10, -1.5) * mm, "end": v(10, -6.5) * mm});
            skLineSegment(sketch, "E16.37.0.3", {"start": v(10, -6.5) * mm, "end": v(11, -6.5) * mm});
            skLineSegment(sketch, "E16.37.0.4", {"start": v(10, -1.5) * mm, "end": v(11, -1.5) * mm});
            skPoint(sketch, "E16.38.0.0", {"position": v(8.5, -4) * mm});
            skLineSegment(sketch, "E16.38.0.1", {"start": v(9, -1.5) * mm, "end": v(9, -6.5) * mm});
            skLineSegment(sketch, "E16.38.0.2", {"start": v(8, -1.5) * mm, "end": v(8, -6.5) * mm});
            skLineSegment(sketch, "E16.38.0.3", {"start": v(8, -6.5) * mm, "end": v(9, -6.5) * mm});
            skLineSegment(sketch, "E16.38.0.4", {"start": v(8, -1.5) * mm, "end": v(9, -1.5) * mm});
            skPoint(sketch, "E16.39.0.0", {"position": v(6.5, -4) * mm});
            skLineSegment(sketch, "E16.39.0.1", {"start": v(7, -1.5) * mm, "end": v(7, -6.5) * mm});
            skLineSegment(sketch, "E16.39.0.2", {"start": v(6, -1.5) * mm, "end": v(6, -6.5) * mm});
            skLineSegment(sketch, "E16.39.0.3", {"start": v(6, -6.5) * mm, "end": v(7, -6.5) * mm});
            skLineSegment(sketch, "E16.39.0.4", {"start": v(6, -1.5) * mm, "end": v(7, -1.5) * mm});
            skLineSegment(sketch, "E16.direction1", {"start": v(84.5, -4) * mm, "end": v(82.5, -4) * mm, "construction": true});
            skSolve(sketch);
        }
        {
            var Q0;
            Q0 = qSketchRegion(id + "F3", true);
            extrude(context, id + "F4", {"entities" : qUnion([Q0]), "operationType" : NewBodyOperationType.REMOVE, "oppositeDirection" : true, "depth" : 1 * mm});
        }
    });
